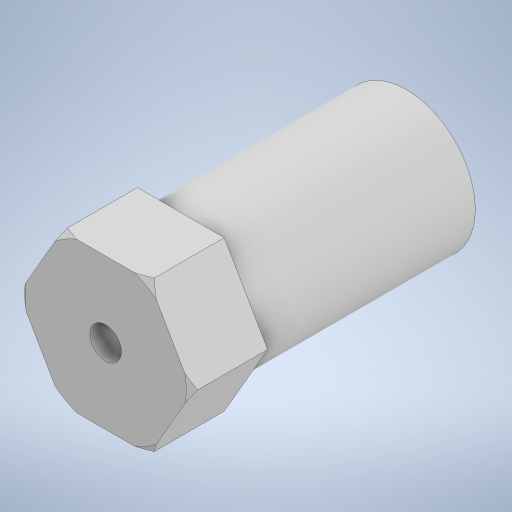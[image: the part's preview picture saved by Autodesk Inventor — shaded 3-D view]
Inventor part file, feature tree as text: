
AUTODESK INVENTOR PART (.ipt)
format: ipt  version: 2024 (Build 280153000, 153)  size: 434,688 bytes
history: native  units: mm
features: sketch x4, extrude x3, revolve x1, chamfer x1
ambient origin geometry x8: Origin, YZ Plane, XZ Plane, XY Plane, X Axis, Y Axis, Z Axis, Center Point
bodies: Body1 (feature_tree)
feature tree (9):
  extrude  "Extrusion6"  Depth=6.0mm TaperAngle=0.0deg
  extrude  "Extrusion7"  Depth=5.1mm
  revolve  "Revolution1"  [1 undecoded]
  chamfer  "Chamfer3"  Distance=18.0mm
  extrude  "Extrusion8"  Depth=6.981317mm
  sketch  "Sketch7"  dims[d24=12.0mm d25=6.0mm d26=0.0mm]
  sketch  "Sketch8"  dims[d27=11.0mm d28=5.1mm]
  sketch  "Sketch9"  dims[d29=4.5mm d30=1.573213mm d31=18.0mm d32=0.0mm]
  sketch  "Sketch10"  dims[d33=0.5mm d35=6.981317mm d38=90.0deg d39=0.125mm d40=0.104887mm d41=1.0mm d42=2.0mm d43=45.0deg d44=2.5mm d45=0.0mm d46=0.0mm]
note: 1 required parameter value undecoded (feature->parameter linkage not recoverable at this tier; creation-order binding heuristic only, values carry confidence <= 0.55)
